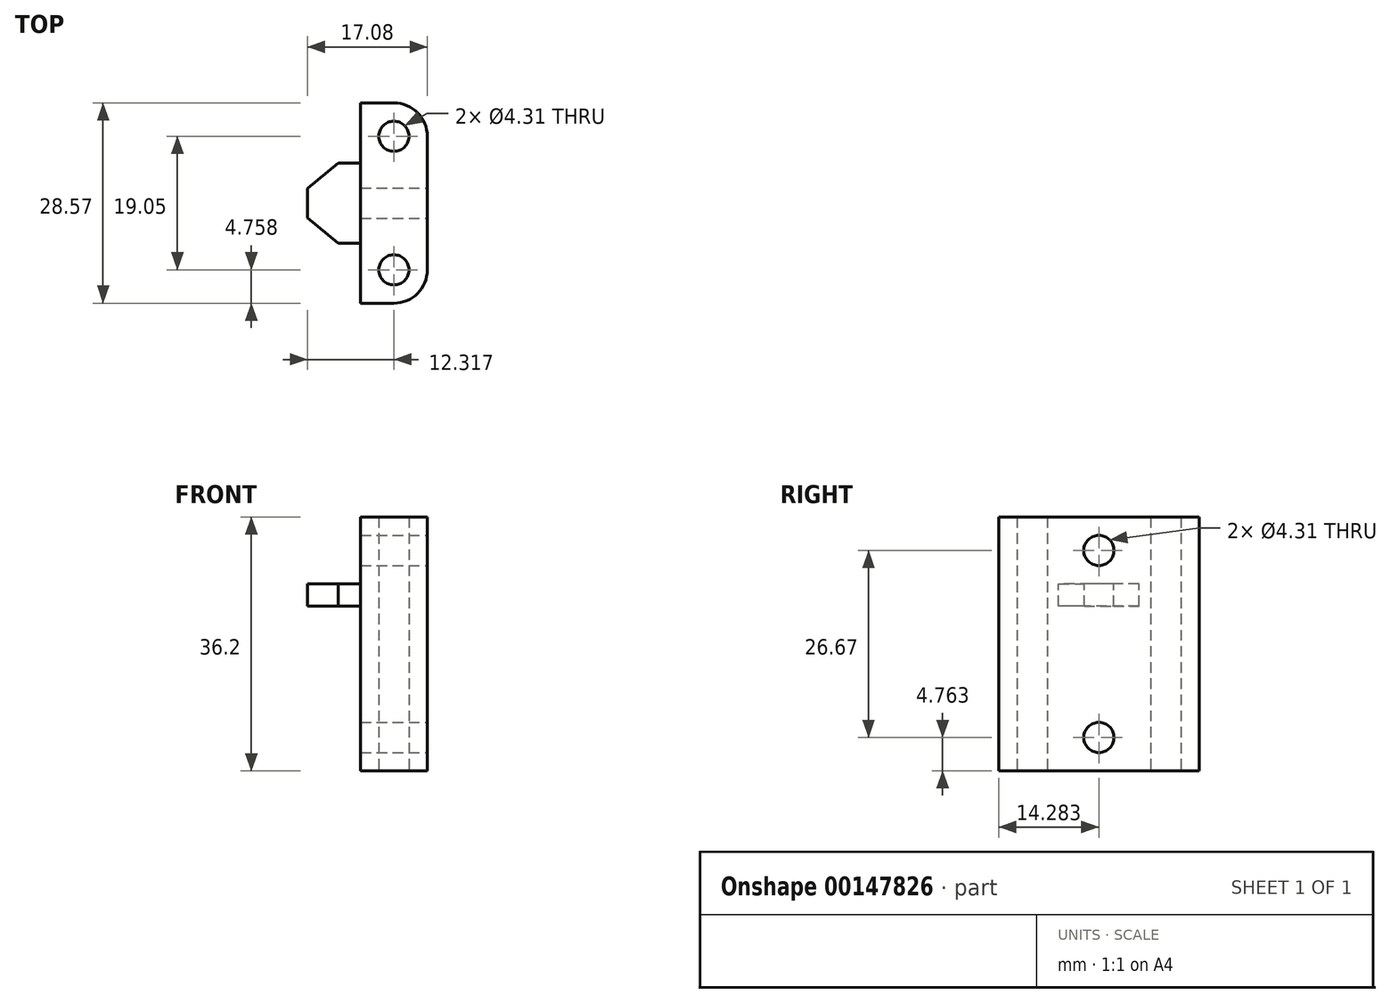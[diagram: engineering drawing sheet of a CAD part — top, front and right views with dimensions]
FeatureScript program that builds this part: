
annotation { "Feature Type Name" : "Feature", "Feature Type Description" : "" }
export const myFeature = defineFeature(function(context is Context, id is Id, definition is map)
    precondition{}
    {
        {
            var Q0;
            Q0=qCreatedBy(makeId("Top.planeOp"),FACE);
            var sketch = newSketch(context, id + "F0", { "sketchPlane" : qUnion([Q0])});
            skLineSegment(sketch, "E0.bottom", {"start": v(0, 0) * mm, "end": v(-9.53, 0) * mm});
            skLineSegment(sketch, "E0.top", {"start": v(0, -28.58) * mm, "end": v(-9.52, -28.58) * mm});
            skLineSegment(sketch, "E0.left", {"start": v(0, 0) * mm, "end": v(0, -28.58) * mm});
            skLineSegment(sketch, "E0.right", {"start": v(-9.52, 0) * mm, "end": v(-9.52, -28.58) * mm});
            skLineSegment(sketch, "E1", {"start": v(-4.76, 0) * mm, "end": v(-4.76, -4.76) * mm, "construction": true});
            skLineSegment(sketch, "E2", {"start": v(-4.76, -4.76) * mm, "end": v(-4.76, -23.81) * mm, "construction": true});
            skLineSegment(sketch, "E3", {"start": v(-4.76, -23.81) * mm, "end": v(-4.76, -28.58) * mm, "construction": true});
            skLineSegment(sketch, "E4", {"start": v(-4.76, -4.76) * mm, "end": v(0, -4.76) * mm, "construction": true});
            skCircle(sketch, "E5", {"center": v(-4.76, -4.76) * mm, "radius": 2.15 * mm});
            skCircle(sketch, "E6", {"center": v(-4.76, -23.81) * mm, "radius": 2.15 * mm});
            skSolve(sketch);
        }
        {
            var Q0;
            Q0=qSketchRegion(id+"F0",true);
            extrude(context, id + "F1", {"entities" : qUnion([Q0]), "depth" : 36.2 * mm});
        }
        {
            var Q0;
            Q0=makeQuery(id+"F1.opExtrude","SWEPT_FACE",FACE,{"disambiguationData":[OSD([sQuery(id+"F0.wireOp",EDGE,"E0.left")])]});
            var sketch = newSketch(context, id + "F2", { "sketchPlane" : qUnion([Q0])});
            skLineSegment(sketch, "E7", {"start": v(-14.29, 36.2) * mm, "end": v(-14.29, 31.43) * mm, "construction": true});
            skLineSegment(sketch, "E8", {"start": v(-14.29, 31.43) * mm, "end": v(-14.29, 4.76) * mm, "construction": true});
            skLineSegment(sketch, "E9", {"start": v(-14.29, 4.76) * mm, "end": v(-14.29, 0) * mm, "construction": true});
            skCircle(sketch, "E10", {"center": v(-14.29, 31.43) * mm, "radius": 2.15 * mm});
            skCircle(sketch, "E11", {"center": v(-14.29, 4.76) * mm, "radius": 2.15 * mm});
            skSolve(sketch);
        }
        {
            var Q0;
            Q0=qSketchRegion(id+"F2",true);
            var Q1;
            Q1=makeQuery(id+"F1.opExtrude","SWEPT_FACE",FACE,{"disambiguationData":[OSD([sQuery(id+"F0.wireOp",EDGE,"E0.right")])]});
            extrude(context, id + "F3", {"entities" : qUnion([Q0]), "operationType" : NewBodyOperationType.REMOVE, "endBound" : BoundingType.UP_TO_SURFACE, "oppositeDirection" : true, "endBoundEntityFace" : qUnion([Q1]), "depth" : 25.4 * mm});
        }
        {
            var Q0;
            Q0=makeQuery(id+"F1.opExtrude","SWEPT_EDGE",EDGE,{"disambiguationData":[OSD([sQuery(id+"F0.wireOp",EDGE,"E0.top"),sQuery(id+"F0.wireOp",EDGE,"E0.left")])]});
            var Q1;
            Q1=makeQuery(id+"F1.opExtrude","SWEPT_EDGE",EDGE,{"disambiguationData":[OSD([sQuery(id+"F0.wireOp",EDGE,"E0.bottom"),sQuery(id+"F0.wireOp",EDGE,"E0.left")])]});
            fillet(context, id + "F4", {"entities" : qUnion([Q0, Q1]), "radius" : 4.76 * mm, "tangentPropagation" : true, "allowEdgeOverflow" : false});
        }
        {
            var Q0;
            Q0=makeQuery(id+"F1.opExtrude","SWEPT_FACE",FACE,{"disambiguationData":[OSD([sQuery(id+"F0.wireOp",EDGE,"E0.right")])]});
            var sketch = newSketch(context, id + "F5", { "sketchPlane" : qUnion([Q0])});
            skLineSegment(sketch, "E12", {"start": v(14.29, 0) * mm, "end": v(14.29, 23.5) * mm, "construction": true});
            skLineSegment(sketch, "E13.bottom", {"start": v(8.56, 23.5) * mm, "end": v(20.02, 23.5) * mm});
            skLineSegment(sketch, "E13.top", {"start": v(8.56, 26.67) * mm, "end": v(20.02, 26.67) * mm});
            skLineSegment(sketch, "E13.left", {"start": v(8.56, 23.5) * mm, "end": v(8.56, 26.67) * mm});
            skLineSegment(sketch, "E13.right", {"start": v(20.02, 23.5) * mm, "end": v(20.02, 26.67) * mm});
            skLineSegment(sketch, "E14", {"start": v(14.29, 26.67) * mm, "end": v(14.29, 31.43) * mm, "construction": true});
            skSolve(sketch);
        }
        {
            var Q0;
            Q0=qSketchRegion(id+"F5",true);
            extrude(context, id + "F6", {"entities" : qUnion([Q0]), "operationType" : NewBodyOperationType.ADD, "depth" : 25.4 * mm});
        }
        {
            var Q0;
            Q0=makeQuery(id+"F6.opExtrude","SWEPT_FACE",FACE,{"disambiguationData":[OSD([sQuery(id+"F5.wireOp",EDGE,"E13.top")])]});
            var sketch = newSketch(context, id + "F7", { "sketchPlane" : qUnion([Q0])});
            skLineSegment(sketch, "E15.bottom", {"start": v(-34.92, -8.56) * mm, "end": v(-12.7, -8.56) * mm});
            skLineSegment(sketch, "E15.top", {"start": v(-34.92, -20.02) * mm, "end": v(-12.7, -20.02) * mm});
            skLineSegment(sketch, "E15.left", {"start": v(-34.92, -8.56) * mm, "end": v(-34.92, -20.02) * mm});
            skLineSegment(sketch, "E15.right", {"start": v(-12.7, -8.56) * mm, "end": v(-12.7, -20.02) * mm, "construction": true});
            skLineSegment(sketch, "E16", {"start": v(-12.7, -8.56) * mm, "end": v(-17.08, -12.2) * mm});
            skLineSegment(sketch, "E17", {"start": v(-12.7, -20.02) * mm, "end": v(-17.08, -16.38) * mm});
            skLineSegment(sketch, "E18", {"start": v(-17.08, -12.2) * mm, "end": v(-17.08, -16.38) * mm});
            skLineSegment(sketch, "E19", {"start": v(-12.7, -14.29) * mm, "end": v(-9.52, -14.29) * mm, "construction": true});
            skLineSegment(sketch, "E20", {"start": v(-12.7, -14.29) * mm, "end": v(-17.08, -14.29) * mm, "construction": true});
            skSolve(sketch);
        }
        {
            var Q0;
            Q0=qSketchRegion(id+"F7",true);
            var Q1;
            Q1=makeQuery(id+"F6.opExtrude","SWEPT_FACE",FACE,{"disambiguationData":[OSD([sQuery(id+"F5.wireOp",EDGE,"E13.bottom")])]});
            extrude(context, id + "F8", {"entities" : qUnion([Q0]), "operationType" : NewBodyOperationType.REMOVE, "endBound" : BoundingType.UP_TO_SURFACE, "oppositeDirection" : true, "endBoundEntityFace" : qUnion([Q1]), "depth" : 25.4 * mm});
        }
    });
